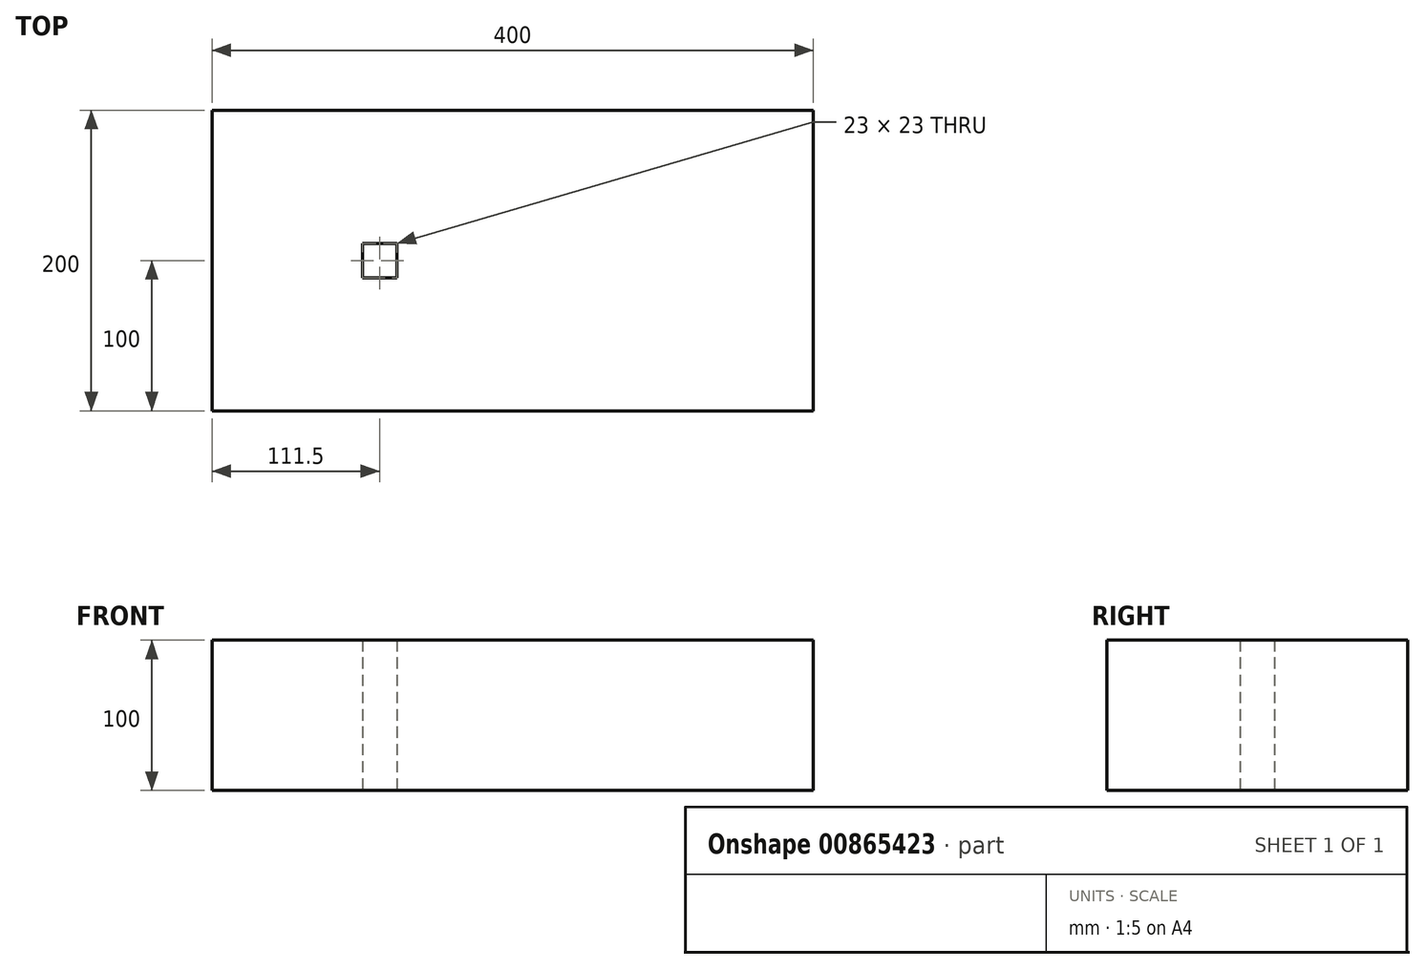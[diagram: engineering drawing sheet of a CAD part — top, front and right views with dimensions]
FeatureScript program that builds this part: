
annotation { "Feature Type Name" : "Feature", "Feature Type Description" : "" }
export const myFeature = defineFeature(function(context is Context, id is Id, definition is map)
    precondition{}
    {
        {
            var Q0;
            Q0=qCreatedBy(makeId("Top.planeOp"),FACE);
            var sketch = newSketch(context, id + "F0", { "sketchPlane" : qUnion([Q0])});
            skLineSegment(sketch, "E0.bottom", {"start": v(0, 0) * mm, "end": v(400, 0) * mm});
            skLineSegment(sketch, "E0.top", {"start": v(0, -200) * mm, "end": v(400, -200) * mm});
            skLineSegment(sketch, "E0.left", {"start": v(0, 0) * mm, "end": v(0, -200) * mm});
            skLineSegment(sketch, "E0.right", {"start": v(400, 0) * mm, "end": v(400, -200) * mm});
            skLineSegment(sketch, "E1.bottom", {"start": v(100, -88.5) * mm, "end": v(123, -88.5) * mm});
            skLineSegment(sketch, "E1.top", {"start": v(100, -111.5) * mm, "end": v(123, -111.5) * mm});
            skLineSegment(sketch, "E1.left", {"start": v(100, -88.5) * mm, "end": v(100, -111.5) * mm});
            skLineSegment(sketch, "E1.right", {"start": v(123, -88.5) * mm, "end": v(123, -111.5) * mm});
            skSolve(sketch);
        }
        {
            var Q0;
            Q0=makeQuery(id+"F0.imprint","IMPRINT",FACE,{"disambiguationData":[TD([[makeQuery(id+"F0.imprint","IMPRINT",EDGE,{"derivedFrom":sQuery(id+"F0.wireOp",EDGE,"E0.bottom")}),-1.0]])]});
            extrude(context, id + "F1", {"entities" : qUnion([Q0]), "depth" : 100 * mm, "offsetDistance" : 25 * mm});
        }
    });
